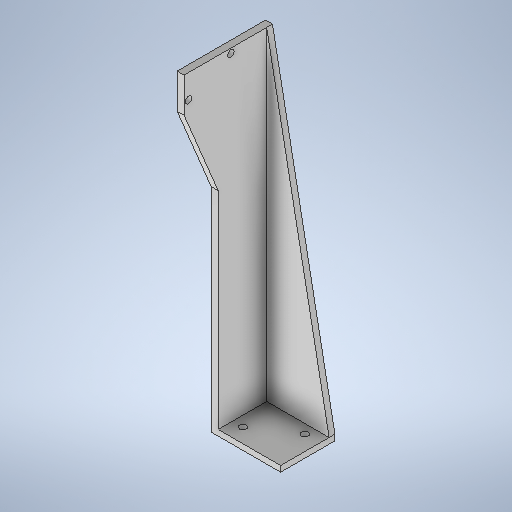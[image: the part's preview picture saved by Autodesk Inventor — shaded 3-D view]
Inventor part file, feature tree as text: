
AUTODESK INVENTOR PART (.ipt)
format: ipt  version: 2025.1 (Build 291241020, 241B)  size: 271,872 bytes
history: native  units: in
note: dims shown in document units (in); Inventor stores cm internally (conversion verified against a paired STEP export)
features: extrude x3, sketch x3
ambient origin geometry x8: Origin, YZ Plane, XZ Plane, XY Plane, X Axis, Y Axis, Z Axis, Center Point
bodies: Solid1 (feature_tree)
feature tree (6):
  extrude  "Extrusion1"  Depth=1.5in
  extrude  "Extrusion2"  Depth=0.15in
  extrude  "Extrusion3"  Depth=0.125in
  sketch  "Sketch1"  dims[d0=1.173in d1=1.5in]
  sketch  "Sketch2"  dims[d2=0.15in d3=0.15in]
  sketch  "Sketch3"  dims[d4=0.313in d5=0.375in d6=0.325in d7=0.325in d8=0.125in d9=0.0in d11=7.0in d12=0.142in d13=0.142in d15=0.512in d16=0.098in d22=157.5deg d24=0.75in d25=1.9105in d26=1.173in d27=0.098in d28=1.012in d29=0.15in d30=0.0in d31=0.125in d32=0.0in]
